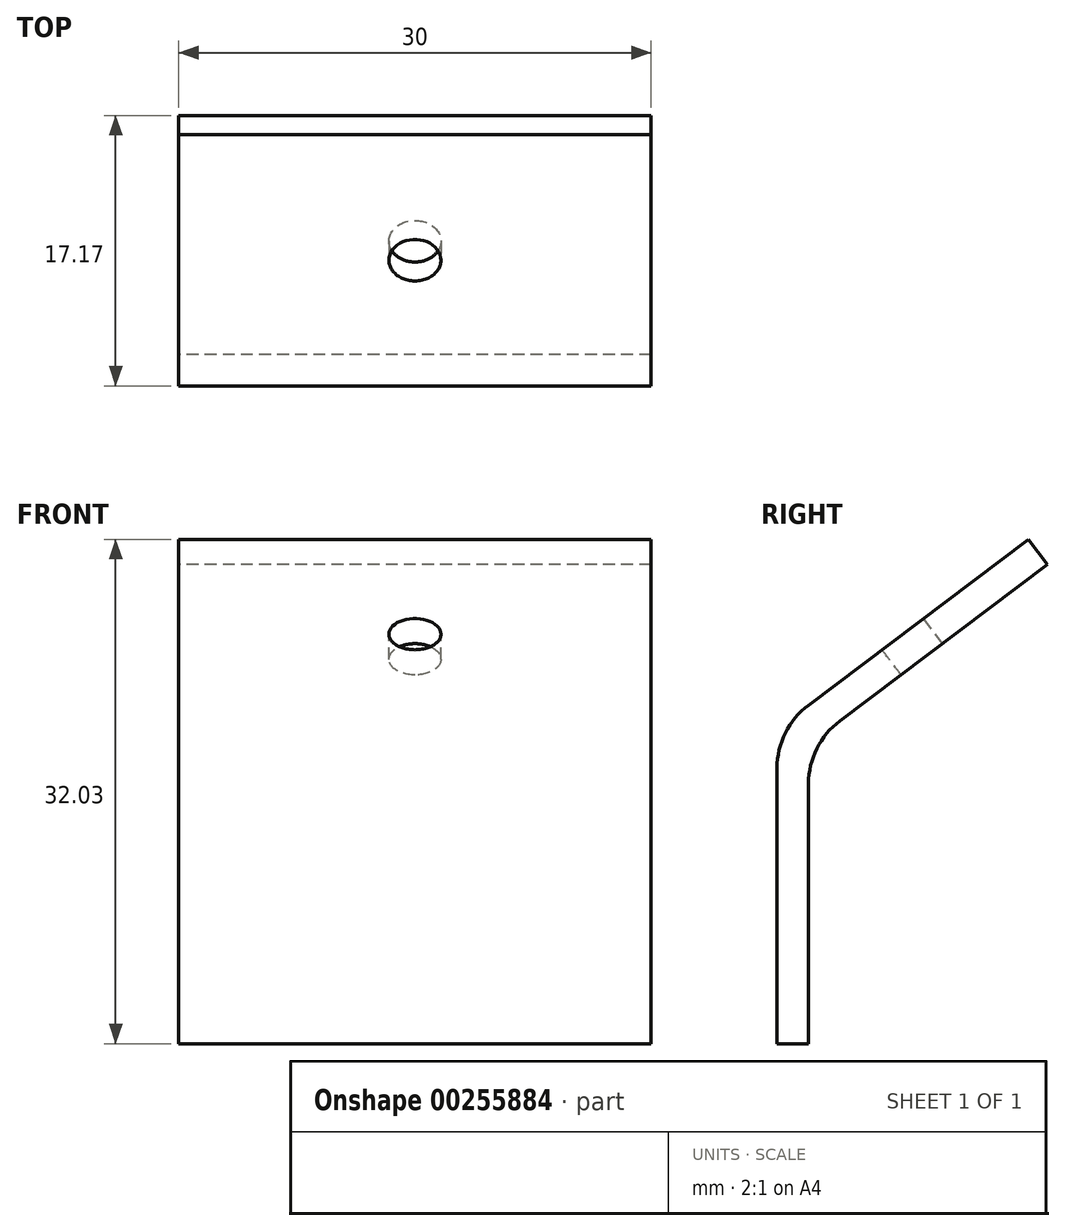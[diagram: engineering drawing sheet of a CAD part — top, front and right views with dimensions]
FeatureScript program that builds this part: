
annotation { "Feature Type Name" : "Feature", "Feature Type Description" : "" }
export const myFeature = defineFeature(function(context is Context, id is Id, definition is map)
    precondition{}
    {
        {
            var Q0;
            Q0=qCreatedBy(makeId("Right.planeOp"),FACE);
            var sketch = newSketch(context, id + "F0", { "sketchPlane" : qUnion([Q0])});
            skLineSegment(sketch, "E0", {"start": v(-15.97, -3.83) * mm, "end": v(-15.97, 16.17) * mm});
            skLineSegment(sketch, "E1", {"start": v(-15.97, 16.17) * mm, "end": v(0, 28.2) * mm});
            skLineSegment(sketch, "E2", {"start": v(0, 28.2) * mm, "end": v(1.2, 26.6) * mm});
            skLineSegment(sketch, "E3", {"start": v(1.2, 26.6) * mm, "end": v(-13.97, 15.17) * mm});
            skLineSegment(sketch, "E4", {"start": v(-13.97, 15.17) * mm, "end": v(-13.97, -3.83) * mm});
            skLineSegment(sketch, "E5", {"start": v(-13.97, -3.83) * mm, "end": v(-15.97, -3.83) * mm});
            skSolve(sketch);
        }
        {
            var Q0;
            Q0 = qSketchRegion(id + "F0", true);
            extrude(context, id + "F1", {"entities" : qUnion([Q0]), "depth" : 30 * mm});
        }
        {
            var Q0;
            Q0=makeQuery(id+"F1.opExtrude","SWEPT_FACE",FACE,{"disambiguationData":[OSD([sQuery(id+"F0.wireOp",EDGE,"E1")])]});
            var sketch = newSketch(context, id + "F2", { "sketchPlane" : qUnion([Q0])});
            skPoint(sketch, "E6", {"position": v(15, 6.97) * mm});
            skLineSegment(sketch, "E7", {"start": v(30, 6.97) * mm, "end": v(0, 6.97) * mm, "construction": true});
            skSolve(sketch);
        }
        {
            var Q0;
            Q0=sQuery(id+"F2.wireOp",VERTEX,"E6");
            var Q1;
            Q1=makeQuery(id+"F1.opExtrude","SWEPT_BODY",BODY,{"disambiguationData":[OSD([sQuery(id+"F0.wireOp",EDGE,"E0"),sQuery(id+"F0.wireOp",EDGE,"E1"),sQuery(id+"F0.wireOp",EDGE,"E2"),sQuery(id+"F0.wireOp",EDGE,"E3"),sQuery(id+"F0.wireOp",EDGE,"E4"),sQuery(id+"F0.wireOp",EDGE,"E5")])]});
            hole(context, id + "F3", {"style" : HoleStyle.SIMPLE, "endStyle" : HoleEndStyle.THROUGH, "holeDiameter" : 3.3 * mm, "tappedDepth" : 12 * mm, "tapClearance" : 3, "startFromSketch" : true, "locations" : qUnion([Q0]), "scope" : qUnion([Q1])});
        }
        {
            var Q0;
            Q0=makeQuery(id+"F1.opExtrude","SWEPT_EDGE",EDGE,{"disambiguationData":[OSD([sQuery(id+"F0.wireOp",EDGE,"E0"),sQuery(id+"F0.wireOp",EDGE,"E1")])]});
            var Q1;
            Q1=makeQuery(id+"F1.opExtrude","SWEPT_EDGE",EDGE,{"disambiguationData":[OSD([sQuery(id+"F0.wireOp",EDGE,"E3"),sQuery(id+"F0.wireOp",EDGE,"E4")])]});
            fillet(context, id + "F4", {"entities" : qUnion([Q0, Q1]), "radius" : 5 * mm, "tangentPropagation" : true, "allowEdgeOverflow" : false});
        }
    });
